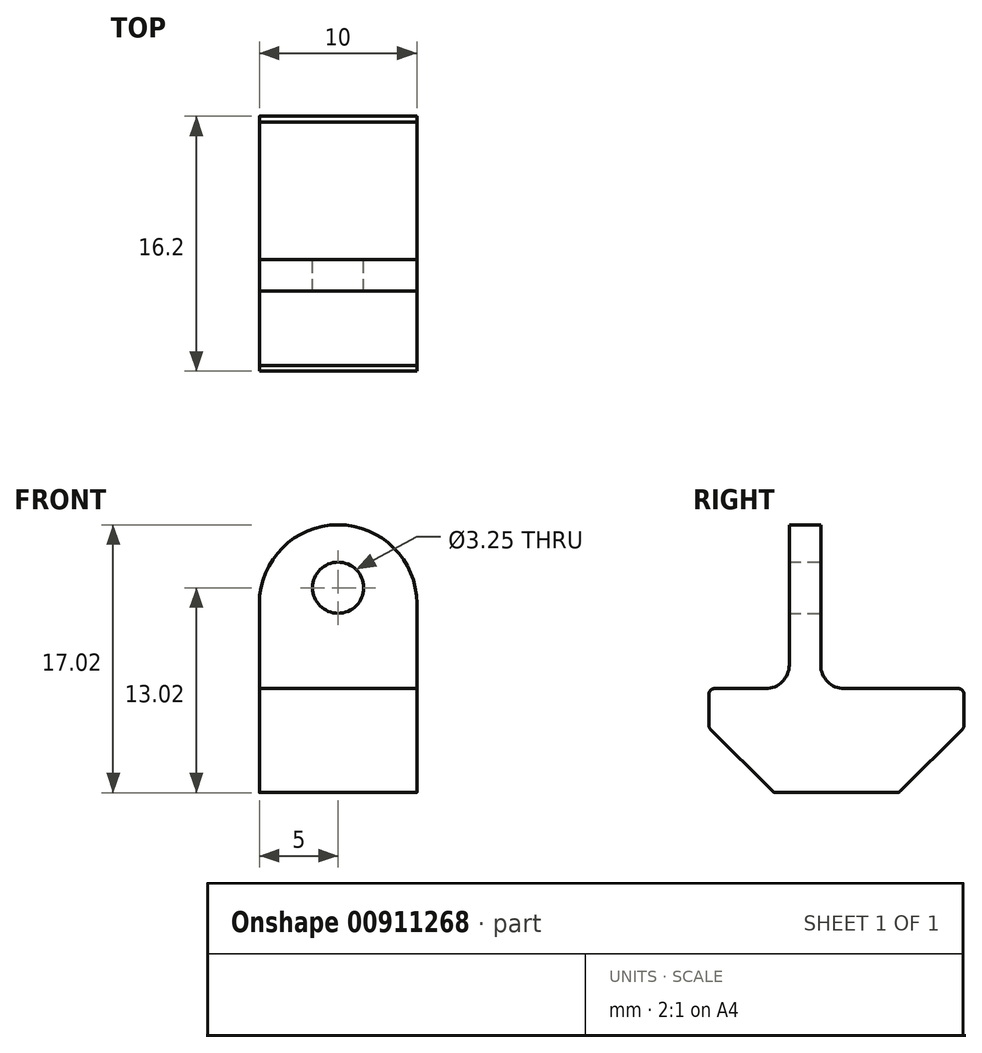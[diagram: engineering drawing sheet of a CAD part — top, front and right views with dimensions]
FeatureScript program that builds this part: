
annotation { "Feature Type Name" : "Feature", "Feature Type Description" : "" }
export const myFeature = defineFeature(function(context is Context, id is Id, definition is map)
    precondition{}
    {
        {
            var Q0;
            Q0=qCreatedBy(makeId("Right.planeOp"),FACE);
            var sketch = newSketch(context, id + "F0", { "sketchPlane" : qUnion([Q0])});
            skArc(sketch, "E0", {"start": v(9.88, 13.7) * mm, "mid": v(9.61, 13.59) * mm, "end": v(9.5, 13.32) * mm});
            skLineSegment(sketch, "E1", {"start": v(12.7, 13.7) * mm, "end": v(9.88, 13.7) * mm});
            skArc(sketch, "E2", {"start": v(13.7, 12.7) * mm, "mid": v(13.4, 13.4) * mm, "end": v(12.7, 13.7) * mm});
            skLineSegment(sketch, "E3", {"start": v(13.7, 9.88) * mm, "end": v(13.7, 12.7) * mm});
            skArc(sketch, "E4", {"start": v(13.32, 9.5) * mm, "mid": v(13.59, 9.61) * mm, "end": v(13.7, 9.88) * mm});
            skLineSegment(sketch, "E5", {"start": v(9.88, 9.5) * mm, "end": v(13.32, 9.5) * mm});
            skArc(sketch, "E6", {"start": v(9.5, 9.88) * mm, "mid": v(9.61, 9.61) * mm, "end": v(9.88, 9.5) * mm});
            skLineSegment(sketch, "E7", {"start": v(9.5, 13.32) * mm, "end": v(9.5, 9.88) * mm});
            skArc(sketch, "E8", {"start": v(-9.5, 13.32) * mm, "mid": v(-9.61, 13.59) * mm, "end": v(-9.88, 13.7) * mm});
            skLineSegment(sketch, "E9", {"start": v(-9.5, 9.88) * mm, "end": v(-9.5, 13.32) * mm});
            skArc(sketch, "E10", {"start": v(-9.88, 9.5) * mm, "mid": v(-9.61, 9.61) * mm, "end": v(-9.5, 9.88) * mm});
            skLineSegment(sketch, "E11", {"start": v(-13.32, 9.5) * mm, "end": v(-9.88, 9.5) * mm});
            skArc(sketch, "E12", {"start": v(-13.7, 9.88) * mm, "mid": v(-13.59, 9.61) * mm, "end": v(-13.32, 9.5) * mm});
            skLineSegment(sketch, "E13", {"start": v(-13.7, 12.7) * mm, "end": v(-13.7, 9.88) * mm});
            skArc(sketch, "E14", {"start": v(-12.7, 13.7) * mm, "mid": v(-13.4, 13.4) * mm, "end": v(-13.7, 12.7) * mm});
            skLineSegment(sketch, "E15", {"start": v(-9.88, 13.7) * mm, "end": v(-12.7, 13.7) * mm});
            skArc(sketch, "E16", {"start": v(-1.5, -3.2) * mm, "mid": v(0, -3.53) * mm, "end": v(1.5, -3.2) * mm});
            skLineSegment(sketch, "E17", {"start": v(-2.47, -3.98) * mm, "end": v(-1.5, -3.2) * mm});
            skArc(sketch, "E18", {"start": v(-3.98, -2.47) * mm, "mid": v(-3.9, -3.9) * mm, "end": v(-2.47, -3.98) * mm});
            skLineSegment(sketch, "E19", {"start": v(-3.2, -1.5) * mm, "end": v(-3.98, -2.47) * mm});
            skArc(sketch, "E20", {"start": v(-3.2, 1.5) * mm, "mid": v(-3.53, 0) * mm, "end": v(-3.2, -1.5) * mm});
            skLineSegment(sketch, "E21", {"start": v(-3.98, 2.47) * mm, "end": v(-3.2, 1.5) * mm});
            skArc(sketch, "E22", {"start": v(-2.47, 3.98) * mm, "mid": v(-3.9, 3.9) * mm, "end": v(-3.98, 2.47) * mm});
            skLineSegment(sketch, "E23", {"start": v(-1.5, 3.2) * mm, "end": v(-2.47, 3.98) * mm});
            skArc(sketch, "E24", {"start": v(1.5, 3.2) * mm, "mid": v(0, 3.53) * mm, "end": v(-1.5, 3.2) * mm});
            skLineSegment(sketch, "E25", {"start": v(2.47, 3.98) * mm, "end": v(1.5, 3.2) * mm});
            skArc(sketch, "E26", {"start": v(3.98, 2.47) * mm, "mid": v(3.9, 3.9) * mm, "end": v(2.47, 3.98) * mm});
            skLineSegment(sketch, "E27", {"start": v(3.2, 1.5) * mm, "end": v(3.98, 2.47) * mm});
            skArc(sketch, "E28", {"start": v(3.2, -1.5) * mm, "mid": v(3.53, 0) * mm, "end": v(3.2, 1.5) * mm});
            skLineSegment(sketch, "E29", {"start": v(3.98, -2.47) * mm, "end": v(3.2, -1.5) * mm});
            skArc(sketch, "E30", {"start": v(2.47, -3.98) * mm, "mid": v(3.9, -3.9) * mm, "end": v(3.98, -2.47) * mm});
            skLineSegment(sketch, "E31", {"start": v(1.5, -3.2) * mm, "end": v(2.47, -3.98) * mm});
            skArc(sketch, "E32", {"start": v(-13.32, -9.5) * mm, "mid": v(-13.59, -9.61) * mm, "end": v(-13.7, -9.88) * mm});
            skLineSegment(sketch, "E33", {"start": v(-9.88, -9.5) * mm, "end": v(-13.32, -9.5) * mm});
            skArc(sketch, "E34", {"start": v(-9.5, -9.88) * mm, "mid": v(-9.61, -9.61) * mm, "end": v(-9.88, -9.5) * mm});
            skLineSegment(sketch, "E35", {"start": v(-9.5, -13.32) * mm, "end": v(-9.5, -9.88) * mm});
            skArc(sketch, "E36", {"start": v(-9.88, -13.7) * mm, "mid": v(-9.61, -13.59) * mm, "end": v(-9.5, -13.32) * mm});
            skLineSegment(sketch, "E37", {"start": v(-12.7, -13.7) * mm, "end": v(-9.88, -13.7) * mm});
            skArc(sketch, "E38", {"start": v(-13.7, -12.7) * mm, "mid": v(-13.4, -13.4) * mm, "end": v(-12.7, -13.7) * mm});
            skLineSegment(sketch, "E39", {"start": v(-13.7, -9.88) * mm, "end": v(-13.7, -12.7) * mm});
            skArc(sketch, "E40", {"start": v(9.5, -13.32) * mm, "mid": v(9.61, -13.59) * mm, "end": v(9.88, -13.7) * mm});
            skLineSegment(sketch, "E41", {"start": v(9.5, -9.88) * mm, "end": v(9.5, -13.32) * mm});
            skArc(sketch, "E42", {"start": v(9.88, -9.5) * mm, "mid": v(9.61, -9.61) * mm, "end": v(9.5, -9.88) * mm});
            skLineSegment(sketch, "E43", {"start": v(13.32, -9.5) * mm, "end": v(9.88, -9.5) * mm});
            skArc(sketch, "E44", {"start": v(13.7, -9.88) * mm, "mid": v(13.59, -9.61) * mm, "end": v(13.32, -9.5) * mm});
            skLineSegment(sketch, "E45", {"start": v(13.7, -12.7) * mm, "end": v(13.7, -9.88) * mm});
            skArc(sketch, "E46", {"start": v(12.7, -13.7) * mm, "mid": v(13.4, -13.4) * mm, "end": v(13.7, -12.7) * mm});
            skLineSegment(sketch, "E47", {"start": v(9.88, -13.7) * mm, "end": v(12.7, -13.7) * mm});
            skArc(sketch, "E48", {"start": v(13.24, -4) * mm, "mid": v(12.89, -4.15) * mm, "end": v(12.74, -4.5) * mm});
            skLineSegment(sketch, "E49", {"start": v(12.74, -4.5) * mm, "end": v(12.74, -7.73) * mm});
            skArc(sketch, "E50", {"start": v(12.24, -8.25) * mm, "mid": v(12.6, -8.1) * mm, "end": v(12.74, -7.73) * mm});
            skLineSegment(sketch, "E51", {"start": v(12.24, -8.25) * mm, "end": v(10.26, -8.25) * mm});
            skArc(sketch, "E52", {"start": v(9.9, -8.1) * mm, "mid": v(10.07, -8.21) * mm, "end": v(10.26, -8.25) * mm});
            skLineSegment(sketch, "E53", {"start": v(9.9, -8.1) * mm, "end": v(5.98, -4.18) * mm});
            skArc(sketch, "E54", {"start": v(5.83, -3.82) * mm, "mid": v(5.87, -4.02) * mm, "end": v(5.98, -4.18) * mm});
            skLineSegment(sketch, "E55", {"start": v(5.83, -3.82) * mm, "end": v(5.83, -1.01) * mm});
            skLineSegment(sketch, "E56", {"start": v(5.83, -1.01) * mm, "end": v(5.32, -0.06) * mm});
            skLineSegment(sketch, "E57", {"start": v(5.32, -0.06) * mm, "end": v(5.83, 0.89) * mm});
            skLineSegment(sketch, "E58", {"start": v(5.83, 0.89) * mm, "end": v(5.83, 3.82) * mm});
            skArc(sketch, "E59", {"start": v(5.98, 4.18) * mm, "mid": v(5.87, 4.02) * mm, "end": v(5.83, 3.82) * mm});
            skLineSegment(sketch, "E60", {"start": v(5.98, 4.18) * mm, "end": v(9.9, 8.1) * mm});
            skArc(sketch, "E61", {"start": v(10.26, 8.25) * mm, "mid": v(10.07, 8.21) * mm, "end": v(9.9, 8.1) * mm});
            skLineSegment(sketch, "E62", {"start": v(10.26, 8.25) * mm, "end": v(12.24, 8.25) * mm});
            skArc(sketch, "E63", {"start": v(12.74, 7.73) * mm, "mid": v(12.6, 8.1) * mm, "end": v(12.24, 8.25) * mm});
            skLineSegment(sketch, "E64", {"start": v(12.74, 7.73) * mm, "end": v(12.74, 4.5) * mm});
            skArc(sketch, "E65", {"start": v(12.74, 4.5) * mm, "mid": v(12.89, 4.15) * mm, "end": v(13.24, 4) * mm});
            skLineSegment(sketch, "E66", {"start": v(13.24, 4) * mm, "end": v(14.5, 4) * mm});
            skArc(sketch, "E67", {"start": v(14.5, 4) * mm, "mid": v(14.85, 4.15) * mm, "end": v(15, 4.5) * mm});
            skLineSegment(sketch, "E68", {"start": v(15, 4.5) * mm, "end": v(15, 13) * mm});
            skArc(sketch, "E69", {"start": v(15, 13) * mm, "mid": v(14.41, 14.41) * mm, "end": v(13, 15) * mm});
            skLineSegment(sketch, "E70", {"start": v(13, 15) * mm, "end": v(4.5, 15) * mm});
            skArc(sketch, "E71", {"start": v(4.5, 15) * mm, "mid": v(4.15, 14.85) * mm, "end": v(4, 14.5) * mm});
            skLineSegment(sketch, "E72", {"start": v(4, 14.5) * mm, "end": v(4, 13.24) * mm});
            skArc(sketch, "E73", {"start": v(4, 13.24) * mm, "mid": v(4.15, 12.89) * mm, "end": v(4.5, 12.74) * mm});
            skLineSegment(sketch, "E74", {"start": v(4.5, 12.74) * mm, "end": v(7.73, 12.74) * mm});
            skArc(sketch, "E75", {"start": v(8.25, 12.24) * mm, "mid": v(8.1, 12.6) * mm, "end": v(7.73, 12.74) * mm});
            skLineSegment(sketch, "E76", {"start": v(8.25, 12.24) * mm, "end": v(8.25, 10.26) * mm});
            skArc(sketch, "E77", {"start": v(8.1, 9.9) * mm, "mid": v(8.21, 10.07) * mm, "end": v(8.25, 10.26) * mm});
            skLineSegment(sketch, "E78", {"start": v(8.1, 9.9) * mm, "end": v(4.18, 5.98) * mm});
            skArc(sketch, "E79", {"start": v(3.82, 5.83) * mm, "mid": v(4.02, 5.87) * mm, "end": v(4.18, 5.98) * mm});
            skLineSegment(sketch, "E80", {"start": v(3.82, 5.83) * mm, "end": v(0.95, 5.83) * mm});
            skLineSegment(sketch, "E81", {"start": v(0.95, 5.83) * mm, "end": v(0, 5.32) * mm});
            skLineSegment(sketch, "E82", {"start": v(0, 5.32) * mm, "end": v(-0.95, 5.83) * mm});
            skLineSegment(sketch, "E83", {"start": v(-0.95, 5.83) * mm, "end": v(-3.82, 5.83) * mm});
            skArc(sketch, "E84", {"start": v(-4.18, 5.98) * mm, "mid": v(-4.02, 5.87) * mm, "end": v(-3.82, 5.83) * mm});
            skLineSegment(sketch, "E85", {"start": v(-4.18, 5.98) * mm, "end": v(-8.1, 9.9) * mm});
            skArc(sketch, "E86", {"start": v(-8.25, 10.26) * mm, "mid": v(-8.21, 10.07) * mm, "end": v(-8.1, 9.9) * mm});
            skLineSegment(sketch, "E87", {"start": v(-8.25, 10.26) * mm, "end": v(-8.25, 12.24) * mm});
            skArc(sketch, "E88", {"start": v(-7.73, 12.74) * mm, "mid": v(-8.1, 12.6) * mm, "end": v(-8.25, 12.24) * mm});
            skLineSegment(sketch, "E89", {"start": v(-7.73, 12.74) * mm, "end": v(-4.5, 12.74) * mm});
            skArc(sketch, "E90", {"start": v(-4.5, 12.74) * mm, "mid": v(-4.15, 12.89) * mm, "end": v(-4, 13.24) * mm});
            skLineSegment(sketch, "E91", {"start": v(-4, 13.24) * mm, "end": v(-4, 14.5) * mm});
            skArc(sketch, "E92", {"start": v(-4, 14.5) * mm, "mid": v(-4.15, 14.85) * mm, "end": v(-4.5, 15) * mm});
            skLineSegment(sketch, "E93", {"start": v(-4.5, 15) * mm, "end": v(-13, 15) * mm});
            skArc(sketch, "E94", {"start": v(-13, 15) * mm, "mid": v(-14.41, 14.41) * mm, "end": v(-15, 13) * mm});
            skLineSegment(sketch, "E95", {"start": v(-15, 13) * mm, "end": v(-15, 4.5) * mm});
            skArc(sketch, "E96", {"start": v(-15, 4.5) * mm, "mid": v(-14.85, 4.15) * mm, "end": v(-14.5, 4) * mm});
            skLineSegment(sketch, "E97", {"start": v(-14.5, 4) * mm, "end": v(-13.24, 4) * mm});
            skArc(sketch, "E98", {"start": v(-13.24, 4) * mm, "mid": v(-12.89, 4.15) * mm, "end": v(-12.74, 4.5) * mm});
            skLineSegment(sketch, "E99", {"start": v(-12.74, 4.5) * mm, "end": v(-12.74, 7.73) * mm});
            skArc(sketch, "E100", {"start": v(-12.24, 8.25) * mm, "mid": v(-12.6, 8.1) * mm, "end": v(-12.74, 7.73) * mm});
            skLineSegment(sketch, "E101", {"start": v(-12.24, 8.25) * mm, "end": v(-10.26, 8.25) * mm});
            skArc(sketch, "E102", {"start": v(-9.9, 8.1) * mm, "mid": v(-10.07, 8.21) * mm, "end": v(-10.26, 8.25) * mm});
            skLineSegment(sketch, "E103", {"start": v(-9.9, 8.1) * mm, "end": v(-5.98, 4.18) * mm});
            skArc(sketch, "E104", {"start": v(-5.83, 3.82) * mm, "mid": v(-5.87, 4.02) * mm, "end": v(-5.98, 4.18) * mm});
            skLineSegment(sketch, "E105", {"start": v(-5.83, 3.82) * mm, "end": v(-5.83, 0.89) * mm});
            skLineSegment(sketch, "E106", {"start": v(-5.83, 0.89) * mm, "end": v(-5.32, -0.06) * mm});
            skLineSegment(sketch, "E107", {"start": v(-5.32, -0.06) * mm, "end": v(-5.83, -1.01) * mm});
            skLineSegment(sketch, "E108", {"start": v(-5.83, -1.01) * mm, "end": v(-5.83, -3.82) * mm});
            skArc(sketch, "E109", {"start": v(-5.98, -4.18) * mm, "mid": v(-5.87, -4.02) * mm, "end": v(-5.83, -3.82) * mm});
            skLineSegment(sketch, "E110", {"start": v(-5.98, -4.18) * mm, "end": v(-9.9, -8.1) * mm});
            skArc(sketch, "E111", {"start": v(-10.26, -8.25) * mm, "mid": v(-10.07, -8.21) * mm, "end": v(-9.9, -8.1) * mm});
            skLineSegment(sketch, "E112", {"start": v(-10.26, -8.25) * mm, "end": v(-12.24, -8.25) * mm});
            skArc(sketch, "E113", {"start": v(-12.74, -7.73) * mm, "mid": v(-12.6, -8.1) * mm, "end": v(-12.24, -8.25) * mm});
            skLineSegment(sketch, "E114", {"start": v(-12.74, -7.73) * mm, "end": v(-12.74, -4.5) * mm});
            skArc(sketch, "E115", {"start": v(-12.74, -4.5) * mm, "mid": v(-12.89, -4.15) * mm, "end": v(-13.24, -4) * mm});
            skLineSegment(sketch, "E116", {"start": v(-13.24, -4) * mm, "end": v(-14.5, -4) * mm});
            skArc(sketch, "E117", {"start": v(-14.5, -4) * mm, "mid": v(-14.85, -4.15) * mm, "end": v(-15, -4.5) * mm});
            skLineSegment(sketch, "E118", {"start": v(-15, -4.5) * mm, "end": v(-15, -13) * mm});
            skArc(sketch, "E119", {"start": v(-15, -13) * mm, "mid": v(-14.41, -14.41) * mm, "end": v(-13, -15) * mm});
            skLineSegment(sketch, "E120", {"start": v(-13, -15) * mm, "end": v(-4.5, -15) * mm});
            skArc(sketch, "E121", {"start": v(-4.5, -15) * mm, "mid": v(-4.15, -14.85) * mm, "end": v(-4, -14.5) * mm});
            skLineSegment(sketch, "E122", {"start": v(-4, -14.5) * mm, "end": v(-4, -13.24) * mm});
            skArc(sketch, "E123", {"start": v(-4, -13.24) * mm, "mid": v(-4.15, -12.89) * mm, "end": v(-4.5, -12.74) * mm});
            skLineSegment(sketch, "E124", {"start": v(-4.5, -12.74) * mm, "end": v(-7.73, -12.74) * mm});
            skArc(sketch, "E125", {"start": v(-8.25, -12.24) * mm, "mid": v(-8.1, -12.6) * mm, "end": v(-7.73, -12.74) * mm});
            skLineSegment(sketch, "E126", {"start": v(-8.25, -12.24) * mm, "end": v(-8.25, -10.26) * mm});
            skArc(sketch, "E127", {"start": v(-8.1, -9.9) * mm, "mid": v(-8.21, -10.07) * mm, "end": v(-8.25, -10.26) * mm});
            skLineSegment(sketch, "E128", {"start": v(-8.1, -9.9) * mm, "end": v(-4.18, -5.98) * mm});
            skArc(sketch, "E129", {"start": v(-3.82, -5.83) * mm, "mid": v(-4.02, -5.87) * mm, "end": v(-4.18, -5.98) * mm});
            skLineSegment(sketch, "E130", {"start": v(-3.82, -5.83) * mm, "end": v(-0.95, -5.83) * mm});
            skLineSegment(sketch, "E131", {"start": v(-0.95, -5.83) * mm, "end": v(0, -5.32) * mm});
            skLineSegment(sketch, "E132", {"start": v(0, -5.32) * mm, "end": v(0.95, -5.83) * mm});
            skLineSegment(sketch, "E133", {"start": v(0.95, -5.83) * mm, "end": v(3.82, -5.83) * mm});
            skArc(sketch, "E134", {"start": v(4.18, -5.98) * mm, "mid": v(4.02, -5.87) * mm, "end": v(3.82, -5.83) * mm});
            skLineSegment(sketch, "E135", {"start": v(4.18, -5.98) * mm, "end": v(8.1, -9.9) * mm});
            skArc(sketch, "E136", {"start": v(8.25, -10.26) * mm, "mid": v(8.21, -10.07) * mm, "end": v(8.1, -9.9) * mm});
            skLineSegment(sketch, "E137", {"start": v(8.25, -10.26) * mm, "end": v(8.25, -12.24) * mm});
            skArc(sketch, "E138", {"start": v(7.73, -12.74) * mm, "mid": v(8.1, -12.6) * mm, "end": v(8.25, -12.24) * mm});
            skLineSegment(sketch, "E139", {"start": v(7.73, -12.74) * mm, "end": v(4.5, -12.74) * mm});
            skArc(sketch, "E140", {"start": v(4.5, -12.74) * mm, "mid": v(4.15, -12.89) * mm, "end": v(4, -13.24) * mm});
            skLineSegment(sketch, "E141", {"start": v(4, -13.24) * mm, "end": v(4, -14.5) * mm});
            skArc(sketch, "E142", {"start": v(4, -14.5) * mm, "mid": v(4.15, -14.85) * mm, "end": v(4.5, -15) * mm});
            skLineSegment(sketch, "E143", {"start": v(4.5, -15) * mm, "end": v(13, -15) * mm});
            skArc(sketch, "E144", {"start": v(13, -15) * mm, "mid": v(14.41, -14.41) * mm, "end": v(15, -13) * mm});
            skLineSegment(sketch, "E145", {"start": v(15, -13) * mm, "end": v(15, -4.5) * mm});
            skArc(sketch, "E146", {"start": v(15, -4.5) * mm, "mid": v(14.85, -4.15) * mm, "end": v(14.5, -4) * mm});
            skLineSegment(sketch, "E147", {"start": v(14.5, -4) * mm, "end": v(13.24, -4) * mm});
            skSolve(sketch);
        }
        {
            var Q0;
            Q0=qCreatedBy(makeId("Right.planeOp"),FACE);
            var sketch = newSketch(context, id + "F1", { "sketchPlane" : qUnion([Q0])});
            skLineSegment(sketch, "E148.0", {"start": v(-7.74, 12.6) * mm, "end": v(-4.5, 12.6) * mm});
            skArc(sketch, "E148.1", {"start": v(-7.74, 12.6) * mm, "mid": v(-8, 12.5) * mm, "end": v(-8.1, 12.24) * mm});
            skLineSegment(sketch, "E148.2", {"start": v(-8.1, 10.26) * mm, "end": v(-8.1, 12.24) * mm});
            skLineSegment(sketch, "E148.3", {"start": v(-0.95, 5.98) * mm, "end": v(-3.82, 5.98) * mm});
            skArc(sketch, "E148.4", {"start": v(-4.07, 6.09) * mm, "mid": v(-3.96, 6.01) * mm, "end": v(-3.82, 5.98) * mm});
            skLineSegment(sketch, "E148.5", {"start": v(-4.07, 6.09) * mm, "end": v(-8, 10.01) * mm});
            skArc(sketch, "E148.6", {"start": v(-8.1, 10.26) * mm, "mid": v(-8.07, 10.13) * mm, "end": v(-8, 10.01) * mm});
            skLineSegment(sketch, "E149.0", {"start": v(3.82, 5.98) * mm, "end": v(0.95, 5.98) * mm});
            skArc(sketch, "E149.1", {"start": v(3.82, 5.98) * mm, "mid": v(3.96, 6.01) * mm, "end": v(4.07, 6.09) * mm});
            skLineSegment(sketch, "E149.2", {"start": v(8, 10.01) * mm, "end": v(4.07, 6.09) * mm});
            skLineSegment(sketch, "E149.3", {"start": v(4.5, 12.6) * mm, "end": v(7.74, 12.6) * mm});
            skArc(sketch, "E149.4", {"start": v(8.1, 12.24) * mm, "mid": v(8, 12.5) * mm, "end": v(7.74, 12.6) * mm});
            skLineSegment(sketch, "E149.5", {"start": v(8.1, 12.24) * mm, "end": v(8.1, 10.26) * mm});
            skArc(sketch, "E149.6", {"start": v(8, 10.01) * mm, "mid": v(8.07, 10.13) * mm, "end": v(8.1, 10.26) * mm});
            skLineSegment(sketch, "E150", {"start": v(-4.5, 12.6) * mm, "end": v(-3, 12.6) * mm});
            skLineSegment(sketch, "E151", {"start": v(-0.95, 5.98) * mm, "end": v(0.95, 5.98) * mm});
            skLineSegment(sketch, "E152", {"start": v(-3, 12.6) * mm, "end": v(-3, 23) * mm});
            skLineSegment(sketch, "E153", {"start": v(-3, 23) * mm, "end": v(-1, 23) * mm});
            skLineSegment(sketch, "E154", {"start": v(-1, 23) * mm, "end": v(-1, 12.6) * mm});
            skLineSegment(sketch, "E155.trimOffspring", {"start": v(-1, 12.6) * mm, "end": v(4.5, 12.6) * mm});
            skSolve(sketch);
        }
        {
            var Q0;
            Q0=makeQuery(id+"F1.imprint","IMPRINT",FACE,{"disambiguationData":[TD([[makeQuery(id+"F1.imprint","IMPRINT",EDGE,{"derivedFrom":sQuery(id+"F1.wireOp",EDGE,"E148.0")}),-1.0]])]});
            extrude(context, id + "F2", {"entities" : qUnion([Q0]), "endBound" : BoundingType.SYMMETRIC, "depth" : 10 * mm, "offsetDistance" : 25 * mm});
        }
        {
            var Q0;
            Q0=makeQuery(id+"F2.opExtrude","SWEPT_EDGE",EDGE,{"disambiguationData":[OSD([sQuery(id+"F1.wireOp",EDGE,"E150"),sQuery(id+"F1.wireOp",EDGE,"E152")])]});
            var Q1;
            Q1=makeQuery(id+"F2.opExtrude","SWEPT_EDGE",EDGE,{"disambiguationData":[OSD([sQuery(id+"F1.wireOp",EDGE,"E154"),sQuery(id+"F1.wireOp",EDGE,"E155.trimOffspring")])]});
            fillet(context, id + "F3", {"entities" : qUnion([Q0, Q1]), "radius" : 1.5 * mm, "tangentPropagation" : true, "allowEdgeOverflow" : false});
        }
        {
            var Q0;
            Q0=makeQuery(id+"F2.opExtrude","CAP_EDGE",EDGE,{"disambiguationData":[OSD([sQuery(id+"F1.wireOp",EDGE,"E153")])],"isStart":false});
            var Q1;
            Q1=makeQuery(id+"F2.opExtrude","CAP_EDGE",EDGE,{"disambiguationData":[OSD([sQuery(id+"F1.wireOp",EDGE,"E153")])],"isStart":true});
            fillet(context, id + "F4", {"entities" : qUnion([Q0, Q1]), "radius" : 5 * mm, "tangentPropagation" : true, "allowEdgeOverflow" : false});
        }
        {
            var Q0;
            Q0=makeQuery(id+"F2.opExtrude","SWEPT_FACE",FACE,{"disambiguationData":[OSD([sQuery(id+"F1.wireOp",EDGE,"E154")])]});
            var sketch = newSketch(context, id + "F5", { "sketchPlane" : qUnion([Q0])});
            skLineSegment(sketch, "E156", {"start": v(0, 23) * mm, "end": v(0, 12.6) * mm, "construction": true});
            skPoint(sketch, "E157", {"position": v(0, 19) * mm});
            skPoint(sketch, "E158.0", {"position": v(0, 15) * mm});
            skSolve(sketch);
        }
        {
            var Q0;
            Q0=sQuery(id+"F5.wireOp",VERTEX,"E157");
            var Q1;
            Q1=makeQuery(id+"F2.opExtrude","SWEPT_BODY",BODY,{"disambiguationData":[OSD([sQuery(id+"F1.wireOp",EDGE,"E148.0"),sQuery(id+"F1.wireOp",EDGE,"E148.1"),sQuery(id+"F1.wireOp",EDGE,"E148.2"),sQuery(id+"F1.wireOp",EDGE,"E148.3"),sQuery(id+"F1.wireOp",EDGE,"E148.4"),sQuery(id+"F1.wireOp",EDGE,"E148.5"),sQuery(id+"F1.wireOp",EDGE,"E148.6"),sQuery(id+"F1.wireOp",EDGE,"E149.0"),sQuery(id+"F1.wireOp",EDGE,"E149.1"),sQuery(id+"F1.wireOp",EDGE,"E149.2"),sQuery(id+"F1.wireOp",EDGE,"E149.3"),sQuery(id+"F1.wireOp",EDGE,"E149.4"),sQuery(id+"F1.wireOp",EDGE,"E149.5"),sQuery(id+"F1.wireOp",EDGE,"E149.6"),sQuery(id+"F1.wireOp",EDGE,"E150"),sQuery(id+"F1.wireOp",EDGE,"E151"),sQuery(id+"F1.wireOp",EDGE,"E152"),sQuery(id+"F1.wireOp",EDGE,"E153"),sQuery(id+"F1.wireOp",EDGE,"E154"),sQuery(id+"F1.wireOp",EDGE,"E155.trimOffspring")])]});
            hole(context, id + "F6", {"style" : HoleStyle.SIMPLE, "endStyle" : HoleEndStyle.THROUGH, "holeDiameter" : 3.25 * mm, "majorDiameter" : 5 * mm, "isTappedThrough" : true, "tappedDepth" : 18.5 * mm, "tapClearance" : 3, "locations" : qUnion([Q0]), "scope" : qUnion([Q1])});
        }
    });
